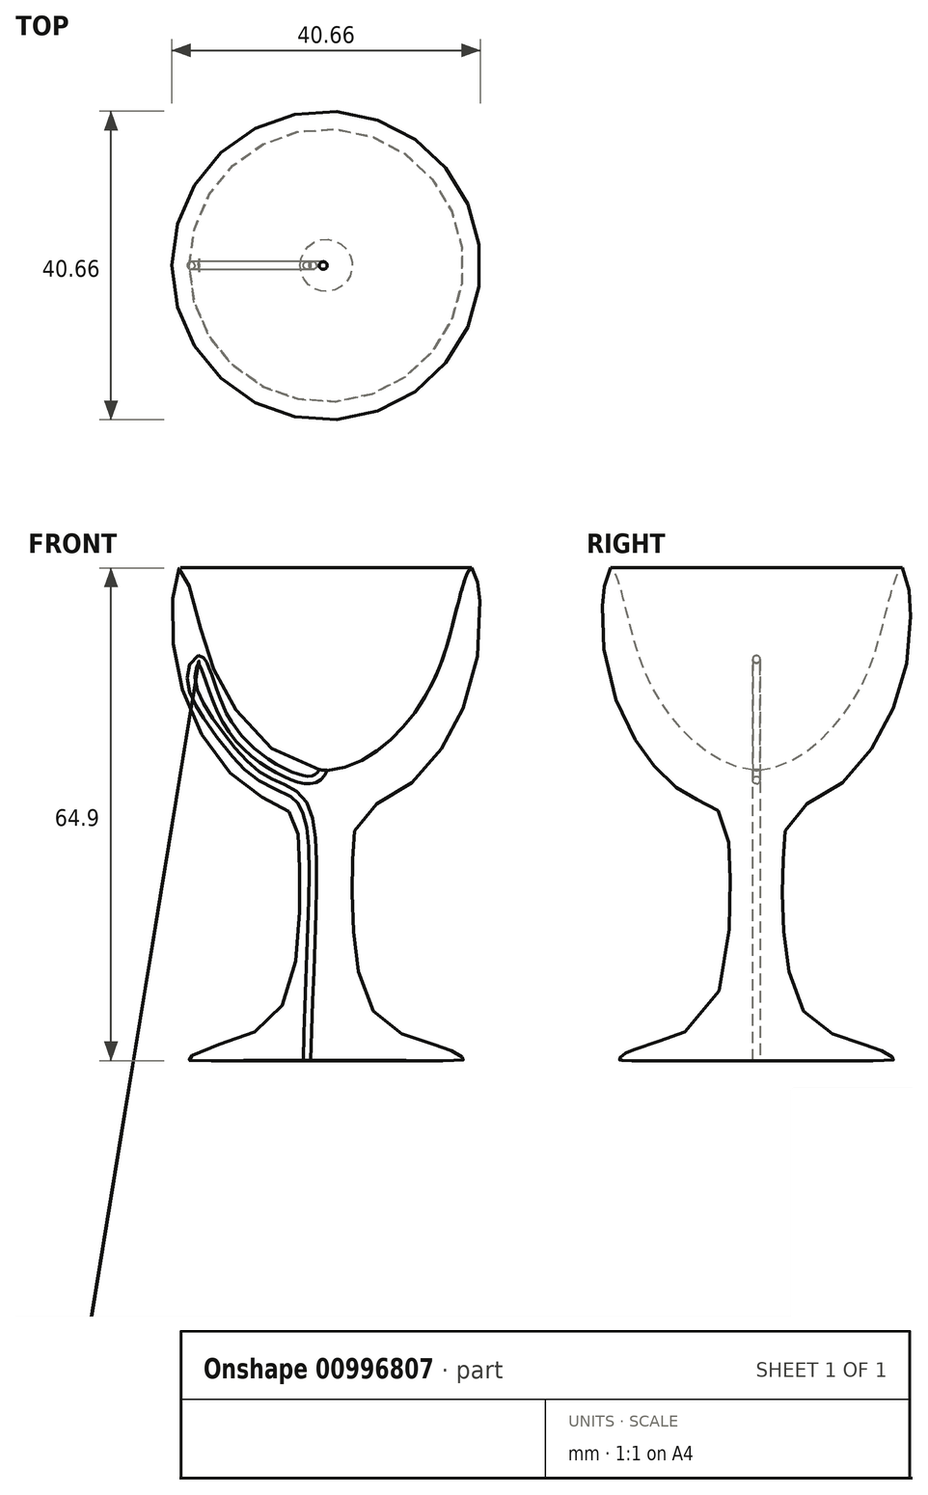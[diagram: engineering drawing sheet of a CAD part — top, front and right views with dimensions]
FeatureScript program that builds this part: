
annotation { "Feature Type Name" : "Feature", "Feature Type Description" : "" }
export const myFeature = defineFeature(function(context is Context, id is Id, definition is map)
    precondition{}
    {
        {
            var Q0;
            Q0=qCreatedBy(makeId("Front.planeOp"),FACE);
            var sketch = newSketch(context, id + "F0", { "sketchPlane" : qUnion([Q0])});
            skFitSpline(sketch, "E0", {"points": [v(0, 3.86) * mm, v(-12.74, 13.1) * mm, v(-16.94, 24.21) * mm, v(-19.19, 30.55) * mm, v(-20.3, 24.96) * mm, v(-17.97, 11.88) * mm, v(-10.12, 1.32) * mm, v(-4.7, -1.75) * mm, v(-3.62, -5.72) * mm, v(-3.54, -16.25) * mm, v(-6.93, -28.8) * mm, v(-14.76, -32.42) * mm, v(-17.97, -34.03) * mm, v(-17.97, -34.23) * mm, v(-18.01, -34.27) * mm, v(0, -34.34) * mm], "startDerivative": vector(-172.05, 11.58) * mm, "endDerivative": vector(490.44, 0) * mm});
            skLineSegment(sketch, "E1", {"start": v(0, 3.86) * mm, "end": v(0, -34.34) * mm});
            skSolve(sketch);
        }
        {
            var Q0;
            Q0=makeQuery(id+"F0.imprint","IMPRINT",FACE,{"disambiguationData":[TD([[makeQuery(id+"F0.imprint","IMPRINT",EDGE,{"derivedFrom":sQuery(id+"F0.wireOp",EDGE,"E0")}),1.0]])]});
            var sketch = newSketch(context, id + "F1", { "sketchPlane" : qUnion([Q0])});
            skFitSpline(sketch, "E2", {"points": [v(0, 5.5) * mm, v(-1, 3.02) * mm, v(-4.3, 3.06) * mm, v(-13.11, 10.33) * mm, v(-16.73, 18.5) * mm, v(-17.79, 16.16) * mm, v(-14.46, 9.22) * mm, v(-8.25, 2.74) * mm, v(-3.43, 0) * mm, v(-1.76, -11.36) * mm, v(-2.55, -36.22) * mm], "startDerivative": vector(0.7, -35.2) * mm, "endDerivative": vector(-2.57, -138.37) * mm});
            skSolve(sketch);
        }
        {
            var Q0;
            Q0=makeQuery(id+"F0.imprint","IMPRINT",FACE,{"disambiguationData":[TD([[makeQuery(id+"F0.imprint","IMPRINT",EDGE,{"derivedFrom":sQuery(id+"F0.wireOp",EDGE,"E0")}),1.0]])]});
            var Q1;
            Q1=sQuery(id+"F0.wireOp",EDGE,"E1");
            revolve(context, id + "F2", {"surfaceOperationType" : NewSurfaceOperationType.NEW, "entities" : qUnion([Q0]), "axis" : qUnion([Q1]), "revolveType" : RevolveType.FULL});
        }
        {
            var Q0;
            Q0=qCreatedBy(makeId("Top.planeOp"),FACE);
            var Q1;
            Q1=sQuery(id+"F1.wireOp",VERTEX,"E2.end");
            cPlane(context, id + "F3", {"entities" : qUnion([Q0, Q1]), "cplaneType" : CPlaneType.PLANE_POINT, "offset" : 25 * mm, "width" : 150 * mm, "height" : 150 * mm});
        }
        {
            var Q0;
            Q0=qCreatedBy(id+"F3.planeOp",FACE);
            var sketch = newSketch(context, id + "F4", { "sketchPlane" : qUnion([Q0])});
            skCircle(sketch, "E3", {"center": v(-2.55, 0) * mm, "radius": 0.5 * mm});
            skSolve(sketch);
        }
        {
            var Q0;
            Q0=makeQuery(id+"F4.imprint","IMPRINT",FACE,{"disambiguationData":[TD([[makeQuery(id+"F4.imprint","IMPRINT",EDGE,{"derivedFrom":sQuery(id+"F4.wireOp",EDGE,"E3")}),1.0]])]});
            var Q1;
            Q1=sQuery(id+"F1.wireOp",EDGE,"E2");
            sweep(context, id + "F5", {"operationType" : NewBodyOperationType.REMOVE, "profiles" : qUnion([Q0]), "path" : qUnion([Q1])});
        }
    });
